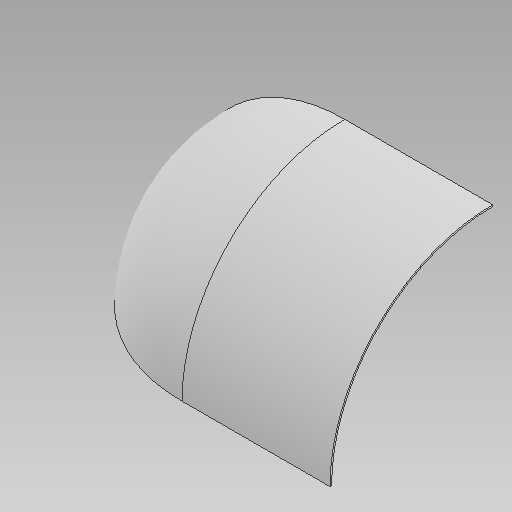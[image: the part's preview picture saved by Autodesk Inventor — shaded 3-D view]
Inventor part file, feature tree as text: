
AUTODESK INVENTOR PART (.ipt)
format: ipt  version: 2021 (Build 250183000, 183)  size: 137,216 bytes
history: native  units: mm
features: sketch x2, revolve x1, extrude x1
ambient origin geometry x8: Origin, YZ Plane, XZ Plane, XY Plane, X Axis, Y Axis, Z Axis, Center Point
bodies: Body1 (feature_tree)
feature tree (4):
  revolve  "Revolution1"  [1 undecoded]
  extrude  "Extrusion2"  TaperAngle=0.0deg  [1 undecoded]
  sketch  "Sketch1"  dims[d0=10.0mm d1=990.0mm]
  sketch  "Sketch2"  dims[d2=0.0mm d3=0.0mm d6=90.0deg d9=900.0mm d10=0.0mm]
note: 2 required parameter values undecoded (feature->parameter linkage not recoverable at this tier; creation-order binding heuristic only, values carry confidence <= 0.55)